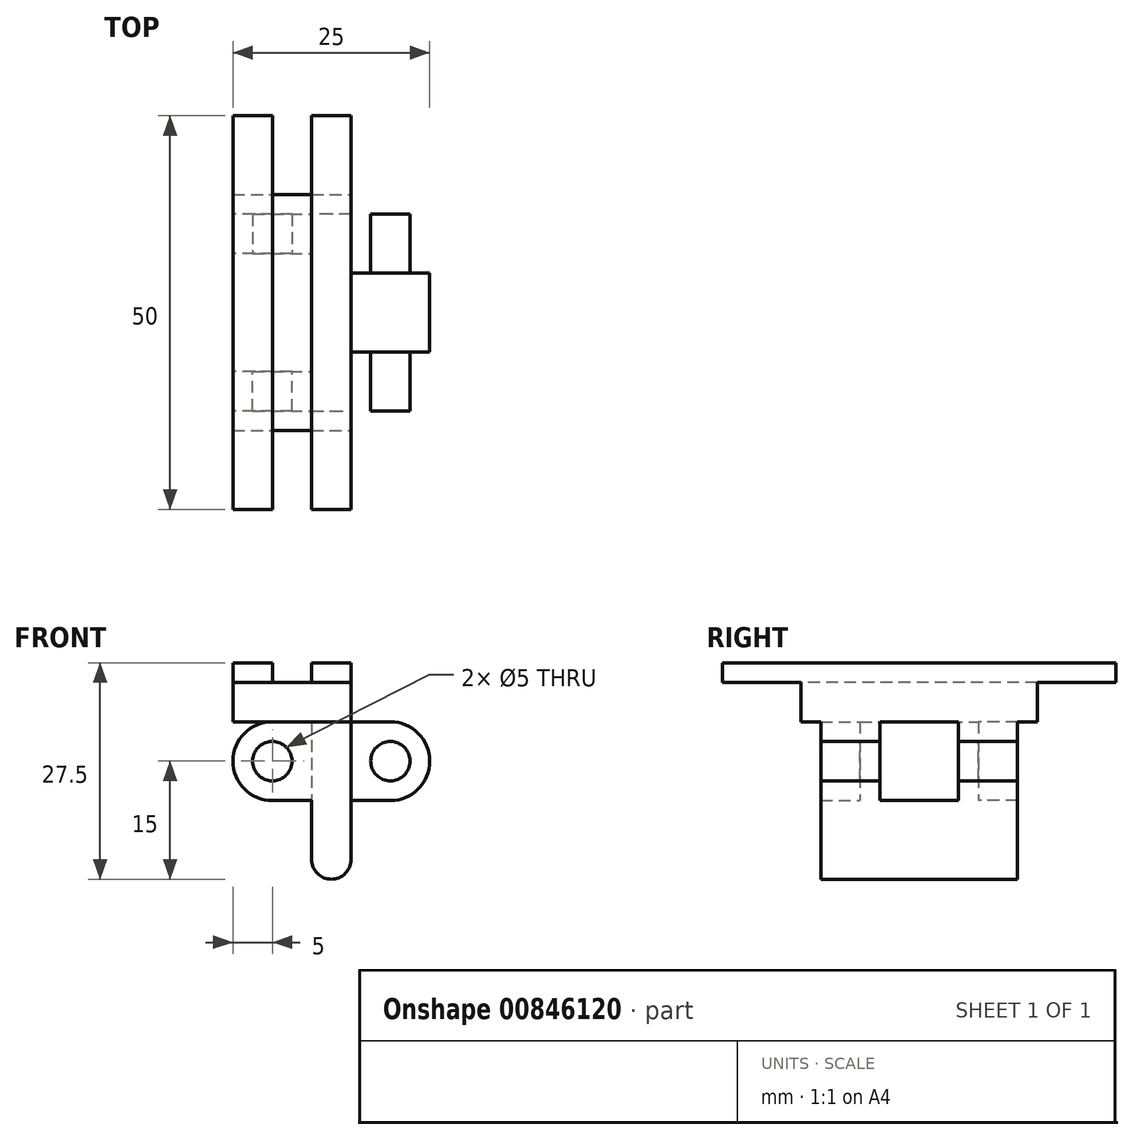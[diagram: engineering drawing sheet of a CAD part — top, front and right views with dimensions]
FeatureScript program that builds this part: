
annotation { "Feature Type Name" : "Feature", "Feature Type Description" : "" }
export const myFeature = defineFeature(function(context is Context, id is Id, definition is map)
    precondition{}
    {
        {
            var Q0;
            Q0=qCreatedBy(makeId("Front.planeOp"),FACE);
            var sketch = newSketch(context, id + "F0", { "sketchPlane" : qUnion([Q0])});
            skCircle(sketch, "E0", {"center": v(0, 0) * mm, "radius": 2.5 * mm});
            skArc(sketch, "E1", {"start": v(0, 5) * mm, "mid": v(-5, 0) * mm, "end": v(0, -5) * mm});
            skLineSegment(sketch, "E2", {"start": v(0, 5) * mm, "end": v(15, 5) * mm});
            skLineSegment(sketch, "E3", {"start": v(0, -5) * mm, "end": v(15, -5) * mm});
            skCircle(sketch, "E4", {"center": v(15, 0) * mm, "radius": 2.5 * mm});
            skArc(sketch, "E5", {"start": v(15, -5) * mm, "mid": v(20, 0) * mm, "end": v(15, 5) * mm});
            skLineSegment(sketch, "E6", {"start": v(5, 5) * mm, "end": v(5, -5) * mm});
            skLineSegment(sketch, "E7", {"start": v(10, 5) * mm, "end": v(10, -5) * mm});
            skSolve(sketch);
        }
        {
            var Q0;
            {var subQ0=sQuery(id+"F0.wireOp",EDGE,"E6");Q0=makeQuery(id+"F0.imprint","IMPRINT",FACE,{"disambiguationData":[TD([[makeQuery(id+"F0.imprint","IMPRINT",EDGE,{"derivedFrom":subQ0}),1.0]])]});}
            var Q1;
            Q1=makeQuery(id+"F0.imprint","IMPRINT",FACE,{"disambiguationData":[TD([[makeQuery(id+"F0.imprint","IMPRINT",EDGE,{"derivedFrom":sQuery(id+"F0.wireOp",EDGE,"E0")}),-1.0]])]});
            extrude(context, id + "F1", {"entities" : qUnion([Q0, Q1]), "depth" : 12.5 * mm, "offsetDistance" : 25 * mm});
        }
        {
            var Q0;
            Q0=makeQuery(id+"F0.imprint","IMPRINT",FACE,{"disambiguationData":[TD([[makeQuery(id+"F0.imprint","IMPRINT",EDGE,{"derivedFrom":sQuery(id+"F0.wireOp",EDGE,"E4")}),-1.0]])]});
            extrude(context, id + "F2", {"entities" : qUnion([Q0]), "operationType" : NewBodyOperationType.ADD, "depth" : 5 * mm, "offsetDistance" : 25 * mm});
        }
        {
            var Q0;
            Q0=makeQuery(id+"F0.imprint","IMPRINT",FACE,{"disambiguationData":[TD([[makeQuery(id+"F0.imprint","IMPRINT",EDGE,{"derivedFrom":sQuery(id+"F0.wireOp",EDGE,"E4")}),1.0]])]});
            extrude(context, id + "F3", {"entities" : qUnion([Q0]), "operationType" : NewBodyOperationType.ADD, "depth" : 12.5 * mm, "offsetDistance" : 25 * mm});
        }
        {
            var Q0;
            Q0=makeQuery(id+"F0.imprint","IMPRINT",FACE,{"disambiguationData":[TD([[makeQuery(id+"F0.imprint","IMPRINT",EDGE,{"derivedFrom":sQuery(id+"F0.wireOp",EDGE,"E0")}),-1.0]])]});
            extrude(context, id + "F4", {"entities" : qUnion([Q0]), "operationType" : NewBodyOperationType.REMOVE, "depth" : 7.5 * mm, "offsetDistance" : 25 * mm});
        }
        {
            var Q0;
            Q0=makeQuery(id+"F1.opExtrude","SWEPT_BODY",BODY,{"disambiguationData":[OSD([sQuery(id+"F0.wireOp",EDGE,"E0"),sQuery(id+"F0.wireOp",EDGE,"E1"),sQuery(id+"F0.wireOp",EDGE,"E2"),sQuery(id+"F0.wireOp",EDGE,"E3"),sQuery(id+"F0.wireOp",EDGE,"E7")])]});
            var Q1;
            Q1=qCreatedBy(makeId("Front.planeOp"),FACE);
            mirror(context, id + "F5", {"operationType" : NewBodyOperationType.ADD, "entities" : qUnion([Q0]), "mirrorPlane" : qUnion([Q1])});
        }
        {
            var Q0;
            {var subQ0=sQuery(id+"F0.wireOp",EDGE,"E3");var subQ1=makeQuery(id+"F2.boolean.opBoolean","MERGE",FACE,{"derivedFrom":[makeQuery(id+"F1.opExtrude","SWEPT_FACE",FACE,{"disambiguationData":[OSD([subQ0])]}),makeQuery(id+"F2.opExtrude","SWEPT_FACE",FACE,{"disambiguationData":[OSD([subQ0])]})]});Q0=makeQuery(id+"F5.boolean.opBoolean","MERGE",FACE,{"derivedFrom":[subQ1,makeQuery(id+"F5.opPattern","COPY",FACE,{"derivedFrom":subQ1,"instanceName":"1"})]});}
            var sketch = newSketch(context, id + "F6", { "sketchPlane" : qUnion([Q0])});
            skLineSegment(sketch, "E8", {"start": v(10, 12.5) * mm, "end": v(10, -12.5) * mm});
            skLineSegment(sketch, "E9", {"start": v(10, -12.5) * mm, "end": v(5, -12.5) * mm});
            skLineSegment(sketch, "E10", {"start": v(5, -12.5) * mm, "end": v(5, 12.5) * mm});
            skLineSegment(sketch, "E11", {"start": v(5, 12.5) * mm, "end": v(10, 12.5) * mm});
            skSolve(sketch);
        }
        {
            var Q0;
            {var subQ0=sQuery(id+"F6.wireOp",EDGE,"E9");Q0=makeQuery(id+"F6.imprint","IMPRINT",FACE,{"disambiguationData":[TD([[makeQuery(id+"F6.imprint","IMPRINT",EDGE,{"derivedFrom":subQ0}),1.0]])]});}
            extrude(context, id + "F7", {"entities" : qUnion([Q0]), "operationType" : NewBodyOperationType.ADD, "depth" : 10 * mm, "offsetDistance" : 25 * mm});
        }
        {
            var Q0;
            Q0=makeQuery(id+"F7.opExtrude","CAP_EDGE",EDGE,{"disambiguationData":[OSD([sQuery(id+"F6.wireOp",EDGE,"E8")])],"isStart":false});
            fillet(context, id + "F8", {"entities" : qUnion([Q0]), "radius" : 2.5 * mm, "tangentPropagation" : true, "allowEdgeOverflow" : false});
        }
        {
            var Q0;
            Q0=makeQuery(id+"F7.opExtrude","CAP_EDGE",EDGE,{"disambiguationData":[OSD([sQuery(id+"F6.wireOp",EDGE,"E10")])],"isStart":false});
            fillet(context, id + "F9", {"entities" : qUnion([Q0]), "radius" : 2.5 * mm, "tangentPropagation" : true, "allowEdgeOverflow" : false});
        }
        {
            var Q0;
            {var subQ0=sQuery(id+"F0.wireOp",EDGE,"E2");var subQ1=makeQuery(id+"F2.boolean.opBoolean","MERGE",FACE,{"derivedFrom":[makeQuery(id+"F1.opExtrude","SWEPT_FACE",FACE,{"disambiguationData":[OSD([subQ0])]}),makeQuery(id+"F2.opExtrude","SWEPT_FACE",FACE,{"disambiguationData":[OSD([subQ0])]})]});Q0=makeQuery(id+"F5.boolean.opBoolean","MERGE",FACE,{"derivedFrom":[subQ1,makeQuery(id+"F5.opPattern","COPY",FACE,{"derivedFrom":subQ1,"instanceName":"1"})]});}
            var sketch = newSketch(context, id + "F10", { "sketchPlane" : qUnion([Q0])});
            skLineSegment(sketch, "E12.bottom", {"start": v(-5, 15) * mm, "end": v(10, 15) * mm});
            skLineSegment(sketch, "E12.top", {"start": v(-5, -15) * mm, "end": v(10, -15) * mm});
            skLineSegment(sketch, "E12.left", {"start": v(-5, 15) * mm, "end": v(-5, -15) * mm});
            skLineSegment(sketch, "E12.right", {"start": v(10, 15) * mm, "end": v(10, -15) * mm});
            skSolve(sketch);
        }
        {
            var Q0;
            Q0 = qSketchRegion(id + "F10", true);
            extrude(context, id + "F11", {"entities" : qUnion([Q0]), "operationType" : NewBodyOperationType.ADD, "depth" : 5 * mm, "offsetDistance" : 25 * mm});
        }
        {
            var Q0;
            Q0=makeQuery(id+"F11.opExtrude","CAP_FACE",FACE,{"disambiguationData":[OSD([sQuery(id+"F10.wireOp",EDGE,"E12.bottom"),sQuery(id+"F10.wireOp",EDGE,"E12.top"),sQuery(id+"F10.wireOp",EDGE,"E12.left"),sQuery(id+"F10.wireOp",EDGE,"E12.right")])],"isStart":false});
            var sketch = newSketch(context, id + "F12", { "sketchPlane" : qUnion([Q0])});
            skLineSegment(sketch, "E13.bottom", {"start": v(-5, 25) * mm, "end": v(0, 25) * mm});
            skLineSegment(sketch, "E13.top", {"start": v(-5, -25) * mm, "end": v(0, -25) * mm});
            skLineSegment(sketch, "E13.left", {"start": v(-5, 25) * mm, "end": v(-5, -25) * mm});
            skLineSegment(sketch, "E13.right", {"start": v(0, 25) * mm, "end": v(0, -25) * mm});
            skLineSegment(sketch, "E14.bottom", {"start": v(10, 25) * mm, "end": v(5, 25) * mm});
            skLineSegment(sketch, "E14.top", {"start": v(10, -25) * mm, "end": v(5, -25) * mm});
            skLineSegment(sketch, "E14.left", {"start": v(10, 25) * mm, "end": v(10, -25) * mm});
            skLineSegment(sketch, "E14.right", {"start": v(5, 25) * mm, "end": v(5, -25) * mm});
            skSolve(sketch);
        }
        {
            var Q0;
            Q0 = qSketchRegion(id + "F12", true);
            extrude(context, id + "F13", {"entities" : qUnion([Q0]), "operationType" : NewBodyOperationType.ADD, "depth" : 2.5 * mm, "offsetDistance" : 25 * mm});
        }
    });
